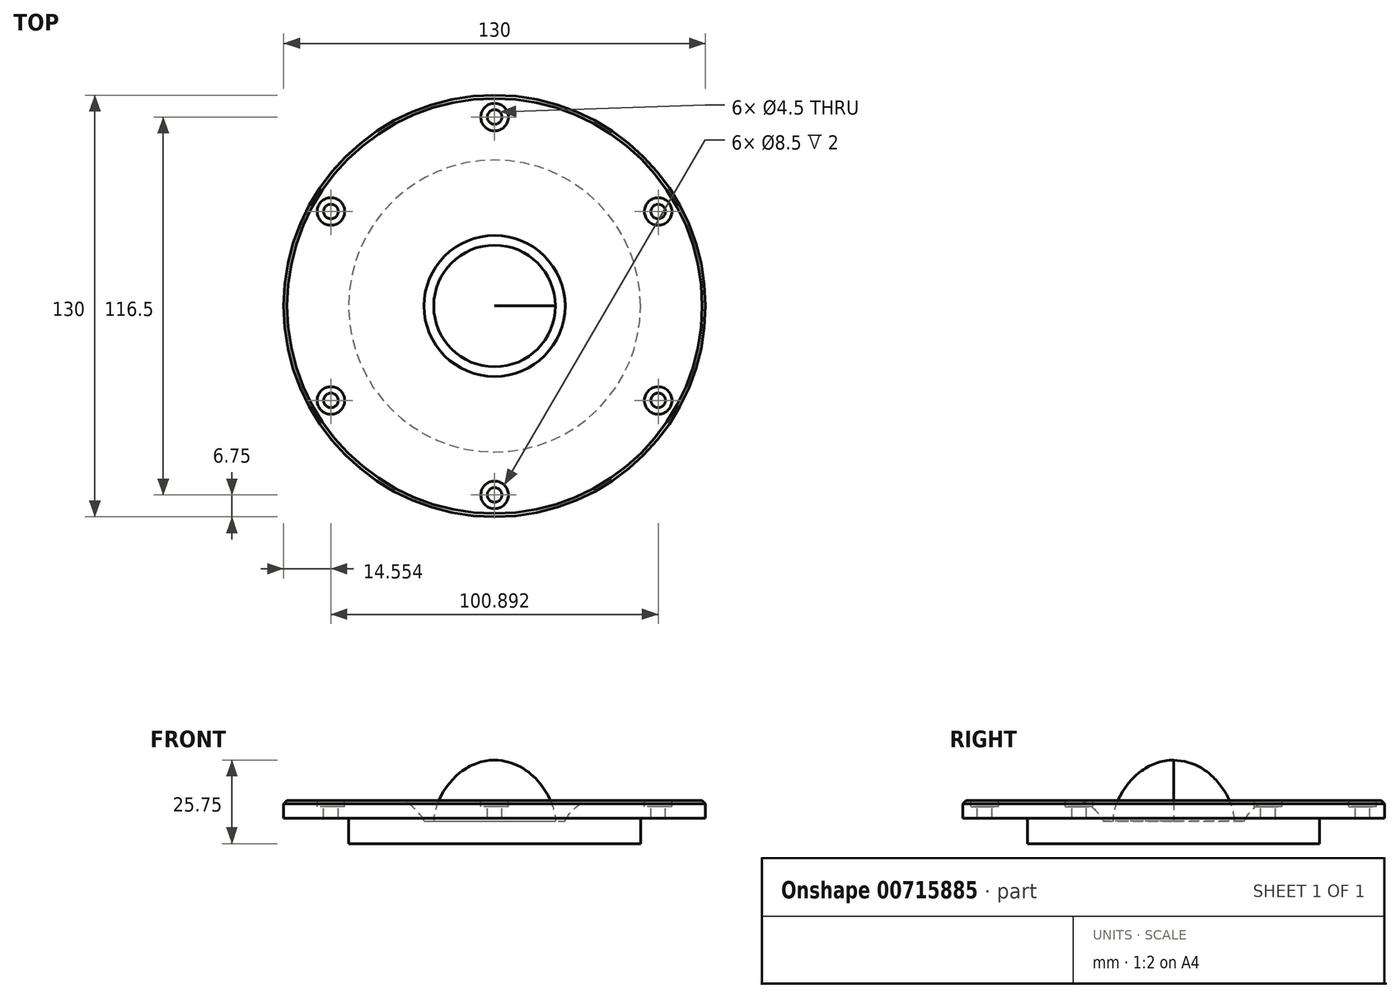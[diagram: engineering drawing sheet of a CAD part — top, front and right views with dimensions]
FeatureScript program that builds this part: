
annotation { "Feature Type Name" : "Feature", "Feature Type Description" : "" }
export const myFeature = defineFeature(function(context is Context, id is Id, definition is map)
    precondition{}
    {
        {
            var Q0;
            Q0=qCreatedBy(makeId("Front.planeOp"),FACE);
            var sketch = newSketch(context, id + "F0", { "sketchPlane" : qUnion([Q0])});
            skPoint(sketch, "E0", {"position": v(65, 0) * mm});
            skLineSegment(sketch, "E1", {"start": v(65, 0) * mm, "end": v(65, -5.5) * mm});
            skFitSpline(sketch, "E2", {"points": [v(0, 12.43) * mm, v(18.75, -6.32) * mm], "startDerivative": vector(35.9, -0.43) * mm, "endDerivative": vector(0, -18.97) * mm});
            skLineSegment(sketch, "E3", {"start": v(18.75, -6.32) * mm, "end": v(21.75, -6.32) * mm});
            skFitSpline(sketch, "E4", {"points": [v(21.75, -6.32) * mm, v(29.29, 0) * mm], "startDerivative": vector(2.4, 6.51) * mm, "endDerivative": vector(8.08, 0) * mm});
            skLineSegment(sketch, "E5", {"start": v(29.29, 0) * mm, "end": v(65, 0) * mm});
            skLineSegment(sketch, "E6", {"start": v(65, -5.5) * mm, "end": v(45, -5.5) * mm});
            skLineSegment(sketch, "E7", {"start": v(45, -5.5) * mm, "end": v(45, -13.32) * mm});
            skLineSegment(sketch, "E8", {"start": v(45, -13.32) * mm, "end": v(0, -13.32) * mm});
            skLineSegment(sketch, "E9", {"start": v(0, -13.32) * mm, "end": v(0, 12.43) * mm});
            skSolve(sketch);
        }
        {
            var Q0;
            Q0=makeQuery(id+"F0.imprint","IMPRINT",FACE,{"disambiguationData":[TD([[makeQuery(id+"F0.imprint","IMPRINT",EDGE,{"derivedFrom":sQuery(id+"F0.wireOp",EDGE,"E1")}),-1.0]])]});
            var Q1;
            Q1=sQuery(id+"F0.wireOp",EDGE,"E9");
            revolve(context, id + "F1", {"surfaceOperationType" : NewSurfaceOperationType.NEW, "entities" : qUnion([Q0]), "axis" : qUnion([Q1]), "revolveType" : RevolveType.FULL});
        }
        {
            var Q0;
            Q0=makeQuery(id+"F1.opRevolve","SWEPT_FACE",FACE,{"disambiguationData":[OSD([sQuery(id+"F0.wireOp",EDGE,"E5")])]});
            var sketch = newSketch(context, id + "F2", { "sketchPlane" : qUnion([Q0])});
            skCircle(sketch, "E10", {"center": v(0, 58.25) * mm, "radius": 2.25 * mm});
            skCircle(sketch, "E11", {"center": v(0, 58.25) * mm, "radius": 4.25 * mm});
            skCircle(sketch, "E12.1.0", {"center": v(-50.45, 29.13) * mm, "radius": 4.25 * mm});
            skCircle(sketch, "E12.1.1", {"center": v(-50.45, 29.13) * mm, "radius": 2.25 * mm});
            skCircle(sketch, "E12.2.0", {"center": v(-50.45, -29.12) * mm, "radius": 4.25 * mm});
            skCircle(sketch, "E12.2.1", {"center": v(-50.45, -29.12) * mm, "radius": 2.25 * mm});
            skCircle(sketch, "E12.3.0", {"center": v(0, -58.25) * mm, "radius": 4.25 * mm});
            skCircle(sketch, "E12.3.1", {"center": v(0, -58.25) * mm, "radius": 2.25 * mm});
            skCircle(sketch, "E12.4.0", {"center": v(50.45, -29.13) * mm, "radius": 4.25 * mm});
            skCircle(sketch, "E12.4.1", {"center": v(50.45, -29.13) * mm, "radius": 2.25 * mm});
            skCircle(sketch, "E12.5.0", {"center": v(50.45, 29.13) * mm, "radius": 4.25 * mm});
            skCircle(sketch, "E12.5.1", {"center": v(50.45, 29.13) * mm, "radius": 2.25 * mm});
            skPoint(sketch, "E12.center", {"position": v(0, 0) * mm});
            skSolve(sketch);
        }
        {
            var Q0;
            Q0=makeQuery(id+"F2.imprint","IMPRINT",FACE,{"disambiguationData":[TD([[makeQuery(id+"F2.imprint","IMPRINT",EDGE,{"derivedFrom":sQuery(id+"F2.wireOp",EDGE,"E12.1.1")}),1.0]])]});
            var Q1;
            Q1=makeQuery(id+"F2.imprint","IMPRINT",FACE,{"disambiguationData":[TD([[makeQuery(id+"F2.imprint","IMPRINT",EDGE,{"derivedFrom":sQuery(id+"F2.wireOp",EDGE,"E10")}),1.0]])]});
            var Q2;
            Q2=makeQuery(id+"F2.imprint","IMPRINT",FACE,{"disambiguationData":[TD([[makeQuery(id+"F2.imprint","IMPRINT",EDGE,{"derivedFrom":sQuery(id+"F2.wireOp",EDGE,"E12.5.1")}),1.0]])]});
            var Q3;
            Q3=makeQuery(id+"F2.imprint","IMPRINT",FACE,{"disambiguationData":[TD([[makeQuery(id+"F2.imprint","IMPRINT",EDGE,{"derivedFrom":sQuery(id+"F2.wireOp",EDGE,"E12.4.1")}),1.0]])]});
            var Q4;
            Q4=makeQuery(id+"F2.imprint","IMPRINT",FACE,{"disambiguationData":[TD([[makeQuery(id+"F2.imprint","IMPRINT",EDGE,{"derivedFrom":sQuery(id+"F2.wireOp",EDGE,"E12.3.1")}),1.0]])]});
            var Q5;
            Q5=makeQuery(id+"F2.imprint","IMPRINT",FACE,{"disambiguationData":[TD([[makeQuery(id+"F2.imprint","IMPRINT",EDGE,{"derivedFrom":sQuery(id+"F2.wireOp",EDGE,"E12.2.1")}),1.0]])]});
            extrude(context, id + "F3", {"entities" : qUnion([Q0, Q1, Q2, Q3, Q4, Q5]), "operationType" : NewBodyOperationType.REMOVE, "oppositeDirection" : true, "depth" : 25 * mm, "offsetDistance" : 25 * mm});
        }
        {
            var Q0;
            Q0=makeQuery(id+"F2.imprint","IMPRINT",FACE,{"disambiguationData":[TD([[makeQuery(id+"F2.imprint","IMPRINT",EDGE,{"derivedFrom":sQuery(id+"F2.wireOp",EDGE,"E12.1.0")}),1.0]])]});
            var Q1;
            Q1=makeQuery(id+"F2.imprint","IMPRINT",FACE,{"disambiguationData":[TD([[makeQuery(id+"F2.imprint","IMPRINT",EDGE,{"derivedFrom":sQuery(id+"F2.wireOp",EDGE,"E10")}),-1.0]])]});
            var Q2;
            Q2=makeQuery(id+"F2.imprint","IMPRINT",FACE,{"disambiguationData":[TD([[makeQuery(id+"F2.imprint","IMPRINT",EDGE,{"derivedFrom":sQuery(id+"F2.wireOp",EDGE,"E12.5.0")}),1.0]])]});
            var Q3;
            Q3=makeQuery(id+"F2.imprint","IMPRINT",FACE,{"disambiguationData":[TD([[makeQuery(id+"F2.imprint","IMPRINT",EDGE,{"derivedFrom":sQuery(id+"F2.wireOp",EDGE,"E12.4.0")}),1.0]])]});
            var Q4;
            Q4=makeQuery(id+"F2.imprint","IMPRINT",FACE,{"disambiguationData":[TD([[makeQuery(id+"F2.imprint","IMPRINT",EDGE,{"derivedFrom":sQuery(id+"F2.wireOp",EDGE,"E12.3.0")}),1.0]])]});
            var Q5;
            Q5=makeQuery(id+"F2.imprint","IMPRINT",FACE,{"disambiguationData":[TD([[makeQuery(id+"F2.imprint","IMPRINT",EDGE,{"derivedFrom":sQuery(id+"F2.wireOp",EDGE,"E12.2.0")}),1.0]])]});
            extrude(context, id + "F4", {"entities" : qUnion([Q0, Q1, Q2, Q3, Q4, Q5]), "operationType" : NewBodyOperationType.REMOVE, "oppositeDirection" : true, "depth" : 2 * mm, "offsetDistance" : 25 * mm});
        }
        {
            var Q0;
            Q0=makeQuery(id+"F1.opRevolve","SWEPT_EDGE",EDGE,{"disambiguationData":[OSD([sQuery(id+"F0.wireOp",EDGE,"E1"),sQuery(id+"F0.wireOp",EDGE,"E5")])]});
            chamfer(context, id + "F5", {"entities" : qUnion([Q0]), "width" : 1 * mm, "tangentPropagation" : true});
        }
    });
